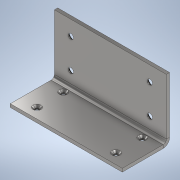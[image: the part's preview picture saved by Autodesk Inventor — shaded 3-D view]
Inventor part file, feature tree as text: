
AUTODESK INVENTOR PART (.ipt)
format: ipt  version: 2021 (Build 250183000, 183)  size: 166,400 bytes
history: native  units: mm
features: sheet_metal_op x4, pattern_linear x3, sketch x3, hole x2, other x2
ambient origin geometry x8: Origin, YZ Plane, XZ Plane, XY Plane, X Axis, Y Axis, Z Axis, Center Point
bodies: Solid1 (feature_tree)
feature tree (14):
  sheet_metal_op  "Face1"
  hole  "Hole1"  [1 undecoded]
  pattern_linear  "Rectangular Pattern1"  Spacing1=5.0mm  [1 undecoded]
  sheet_metal_op  "Flange1"
  hole  "Hole4"  [1 undecoded]
  pattern_linear  "Rectangular Pattern6"  Spacing1=15.5mm  [1 undecoded]
  pattern_linear  "Rectangular Pattern7"  Spacing1=20.594885mm  [1 undecoded]
  sketch  "Sketch1"  dims[d3=170.0mm d4=72.0mm]
  other  "Plate1"
  sketch  "Sketch2"  dims[d5=85.0mm]
  sketch  "Sketch4"  dims[d6=72.0mm d7=5.0mm d8=25.0mm d9=15.5mm d10=6.0mm d11=50.8mm d12=12.0mm d13=2.0mm d14=90.0deg d15=5.0mm d16=20.594885mm d17=20.0mm d19=120.0mm d20=20.0mm d22=40.0mm d38=5.0mm d39=2.5mm d40=10.0mm d41=5.0mm d42=95.0mm d43=90.0deg d44=5.0mm d45=20.0mm d46=5.0mm d47=5.0mm d68=8.0mm d69=6.0mm d70=16.0mm d71=2.0mm d72=90.0deg d73=5.0mm d74=20.594885mm d80=20.0mm d82=120.0mm d83=20.0mm d85=45.0mm d18=20.594885mm d21=0.375mm]
  other  "Plate2"
  sheet_metal_op  "Bend1"
  sheet_metal_op  "Corner1"
note: 5 required parameter values undecoded (feature->parameter linkage not recoverable at this tier; creation-order binding heuristic only, values carry confidence <= 0.55)
